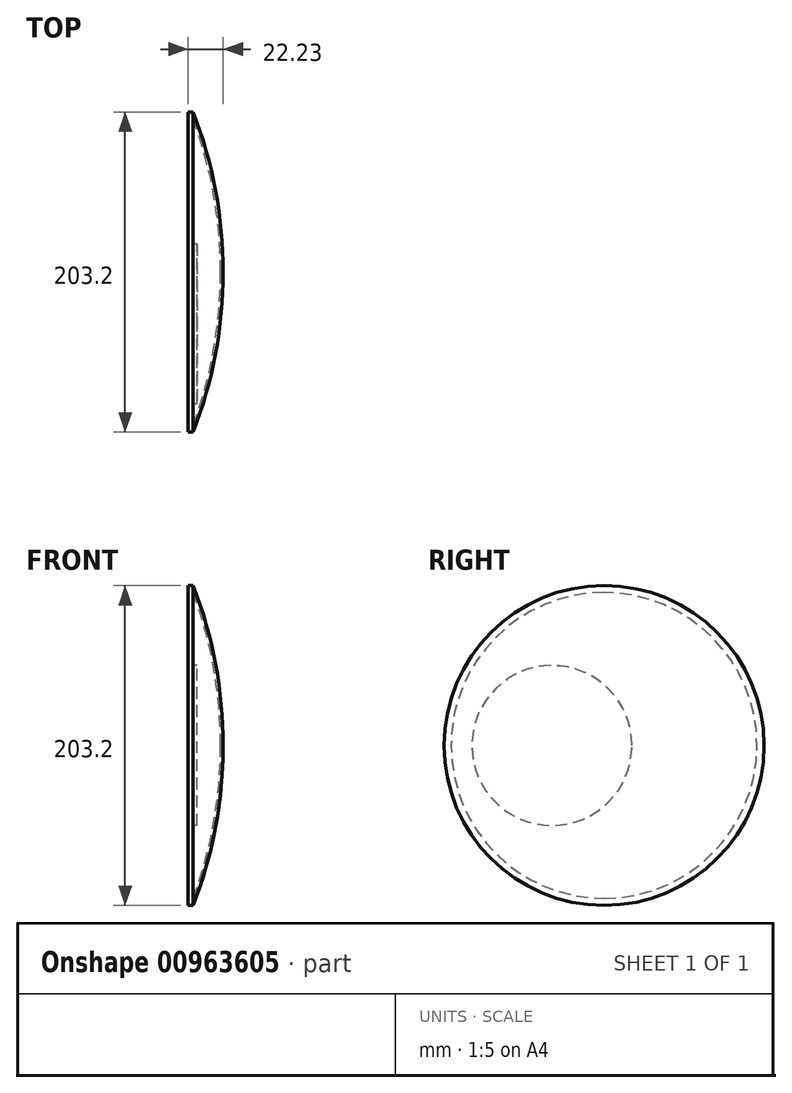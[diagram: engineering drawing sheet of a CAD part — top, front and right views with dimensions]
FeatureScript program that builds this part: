
annotation { "Feature Type Name" : "Feature", "Feature Type Description" : "" }
export const myFeature = defineFeature(function(context is Context, id is Id, definition is map)
    precondition{}
    {
        {
            var Q0;
            Q0=qCreatedBy(makeId("Right.planeOp"),FACE);
            var sketch = newSketch(context, id + "F0", { "sketchPlane" : qUnion([Q0])});
            skCircle(sketch, "E0", {"center": v(0, 0) * mm, "radius": 101.6 * mm});
            skSolve(sketch);
        }
        {
            var Q0;
            Q0 = qSketchRegion(id + "F0", true);
            extrude(context, id + "F1", {"entities" : qUnion([Q0]), "oppositeDirection" : true, "depth" : 3.17 * mm, "offsetDistance" : 25.4 * mm});
        }
        {
            var Q0;
            Q0=qCreatedBy(makeId("Front.planeOp"),FACE);
            var sketch = newSketch(context, id + "F2", { "sketchPlane" : qUnion([Q0])});
            skLineSegment(sketch, "E1.0", {"start": v(0, 101.6) * mm, "end": v(0, -101.6) * mm});
            skArc(sketch, "E2", {"start": v(0, -101.6) * mm, "mid": v(19.05, 0) * mm, "end": v(0, 101.6) * mm});
            skLineSegment(sketch, "E3", {"start": v(19.05, 0) * mm, "end": v(0, 0) * mm});
            skSolve(sketch);
        }
        {
            var Q0;
            {var subQ3=sQuery(id+"F2.wireOp",EDGE,"E3");Q0=makeQuery(id+"F2.imprint","IMPRINT",FACE,{"disambiguationData":[TD([[makeQuery(id+"F2.imprint","IMPRINT",EDGE,{"derivedFrom":subQ3}),-1.0]])]});}
            var Q1;
            Q1=sQuery(id+"F2.wireOp",EDGE,"E3");
            revolve(context, id + "F3", {"surfaceOperationType" : NewSurfaceOperationType.NEW, "entities" : qUnion([Q0]), "axis" : qUnion([Q1]), "revolveType" : RevolveType.FULL});
        }
        {
            var Q0;
            Q0=makeQuery(id+"F3.opRevolve","SWEPT_FACE",FACE,{"disambiguationData":[OSD([sQuery(id+"F2.wireOp",EDGE,"E1.0")])]});
            shell(context, id + "F4", {"entities" : qUnion([Q0]), "thickness" : 1.59 * mm});
        }
        {
            var Q0;
            Q0=makeQuery(id+"F1.opExtrude","CAP_FACE",FACE,{"disambiguationData":[OSD([sQuery(id+"F0.wireOp",EDGE,"E0")])],"isStart":true});
            var sketch = newSketch(context, id + "F5", { "sketchPlane" : qUnion([Q0])});
            skCircle(sketch, "E4", {"center": v(-46.33, 0) * mm, "radius": 50.8 * mm});
            skSolve(sketch);
        }
        {
            var Q0;
            Q0 = qSketchRegion(id + "F5", true);
            extrude(context, id + "F6", {"entities" : qUnion([Q0]), "depth" : 2.54 * mm, "offsetDistance" : 25.4 * mm});
        }
        {
            var Q0;
            Q0=makeQuery(id+"F6.opExtrude","SWEPT_BODY",BODY,{"disambiguationData":[OSD([sQuery(id+"F5.wireOp",EDGE,"E4")])]});
            transform(context, id + "F7", {"entities" : qUnion([Q0]), "transformType" : TransformType.TRANSLATION_3D, "dx" : 0 * mm, "dy" : 13.2 * mm, "dz" : 0 * mm, "makeCopy" : false});
        }
    });
